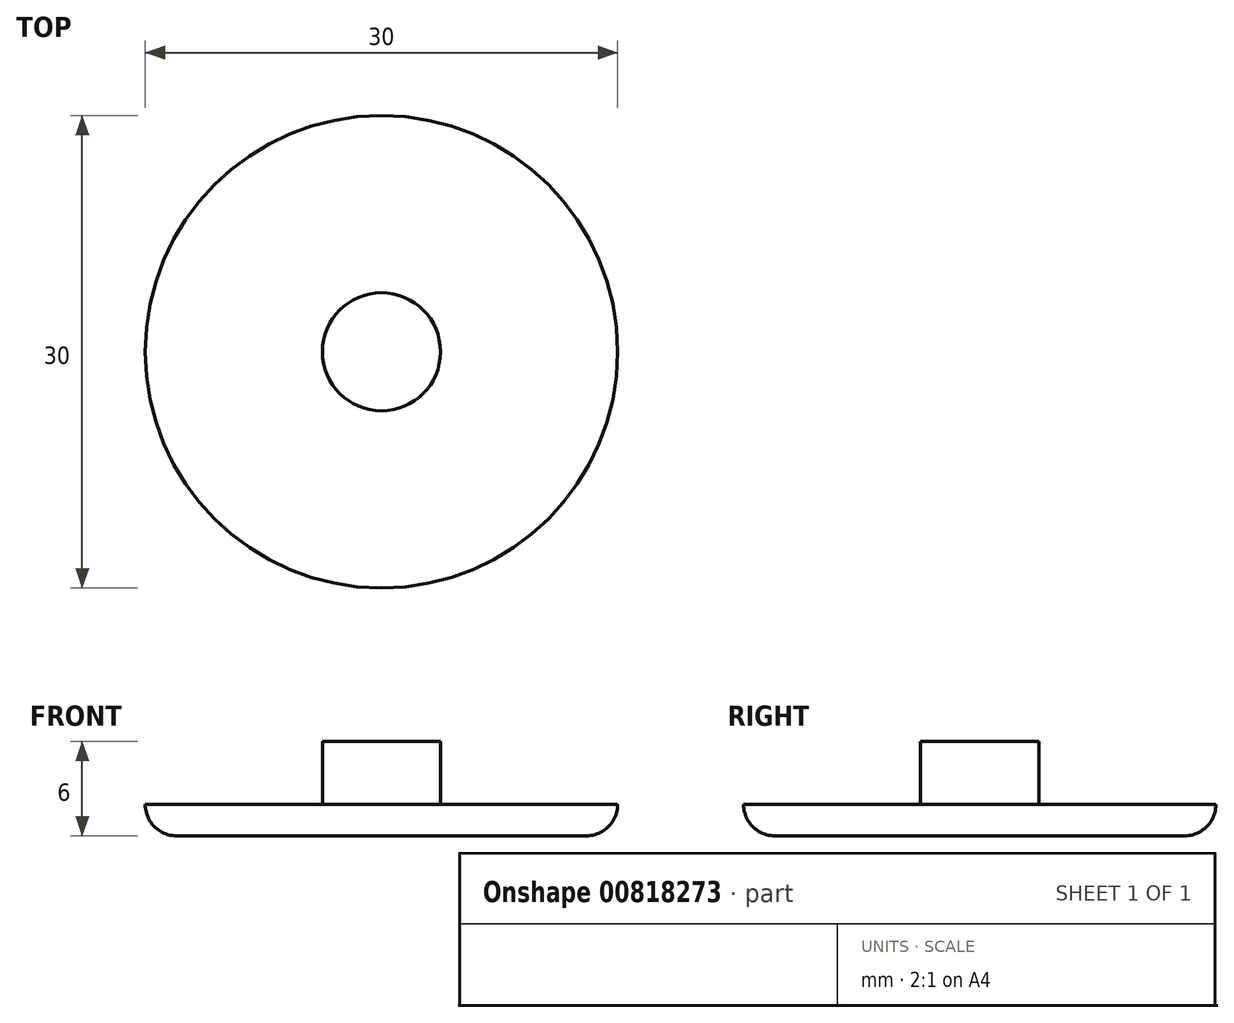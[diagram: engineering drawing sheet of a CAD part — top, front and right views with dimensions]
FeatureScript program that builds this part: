
annotation { "Feature Type Name" : "Feature", "Feature Type Description" : "" }
export const myFeature = defineFeature(function(context is Context, id is Id, definition is map)
    precondition{}
    {
        {
            var Q0;
            Q0=qCreatedBy(makeId("Top.planeOp"),FACE);
            var sketch = newSketch(context, id + "F0", { "sketchPlane" : qUnion([Q0])});
            skCircle(sketch, "E0", {"center": v(0, 0) * mm, "radius": 15 * mm});
            skCircle(sketch, "E1", {"center": v(0, 0) * mm, "radius": 3.75 * mm});
            skSolve(sketch);
        }
        {
            var Q0;
            Q0 = qSketchRegion(id + "F0", true);
            var Q1;
            Q1=makeQuery(id+"F0.imprint","IMPRINT",FACE,{"disambiguationData":[TD([[makeQuery(id+"F0.imprint","IMPRINT",EDGE,{"derivedFrom":sQuery(id+"F0.wireOp",EDGE,"E1")}),1.0]])]});
            extrude(context, id + "F1", {"entities" : qUnion([Q0, Q1]), "depth" : 2 * mm, "offsetDistance" : 25 * mm});
        }
        {
            var Q0;
            Q0=makeQuery(id+"F1.opExtrude","CAP_FACE",FACE,{"disambiguationData":[OSD([sQuery(id+"F0.wireOp",EDGE,"E0")])],"isStart":false});
            var sketch = newSketch(context, id + "F2", { "sketchPlane" : qUnion([Q0])});
            skCircle(sketch, "E2", {"center": v(0, 0) * mm, "radius": 3.75 * mm});
            skSolve(sketch);
        }
        {
            var Q0;
            Q0=makeQuery(id+"F2.imprint","IMPRINT",FACE,{"disambiguationData":[TD([[makeQuery(id+"F2.imprint","IMPRINT",EDGE,{"derivedFrom":sQuery(id+"F2.wireOp",EDGE,"E2")}),1.0]])]});
            extrude(context, id + "F3", {"entities" : qUnion([Q0]), "operationType" : NewBodyOperationType.ADD, "depth" : 4 * mm, "offsetDistance" : 25 * mm});
        }
        {
            var Q0;
            Q0=makeQuery(id+"F1.opExtrude","CAP_EDGE",EDGE,{"disambiguationData":[OSD([sQuery(id+"F0.wireOp",EDGE,"E0")])],"isStart":true});
            fillet(context, id + "F4", {"entities" : qUnion([Q0]), "radius" : 2 * mm, "tangentPropagation" : true, "allowEdgeOverflow" : false});
        }
    });
